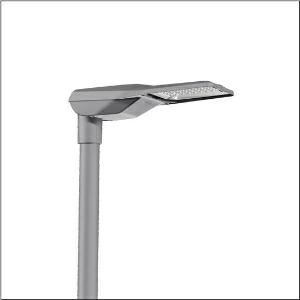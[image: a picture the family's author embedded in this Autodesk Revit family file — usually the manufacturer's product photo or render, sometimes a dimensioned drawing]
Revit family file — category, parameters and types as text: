
# Revit family: streetlight_sl_21_iq_mini___st0_8a_5xe2c31d08hb_f94e
name_source: partatom
category: Lighting Fixtures
units: mm (PartAtom-declared; Revit-internal decimal feet)

## family parameters
Cut with Voids When Loaded = No
Host = Face
Light Source = No
Part Type = Normal
Room Calculation Point = No
Round Connector Dimension = Use Diameter
Shared = No

## types (1)
- --- (1 x LED, 9450 lm, 70.9 W, 3000K)
    Apparent Load = 71 VA
    CIE Flux Codes = 38 75 97 100 100
    Color Rendering = 70
    Color Temperature = 3000K
    Default Elevation = 1800 mm
    Description = Streetlight SL 21 iQ mini, mast luminaire, primary light control with lens, of PMMA, primary optical cover: cover, of toughened safety glass, transparent, light distribution: ST0.8a, light emission: direct distribution, primary light characteristic: asymmetric, installation type: post-top, side-entry, LED, High Power LED, rated luminous flux: 9.450lm, luminous efficacy: 133lm/W, light colour: 730, colour temperature: 3000K, control: Auto-Match, Temp-Guard, Lumen-Switch, Night-Set, Smart-Wire, Light-Fading, Desk-Remote (wireless, voltage-free reading and setting of iQ features in the workshop via application-optimized NFC function/RFID function), optimised constant luminous flux control (CLO 2.0), presetting dimming linear, mains connection: 220..240V, AC, 50/60Hz, start of lifetime: 71W, end of service life: 75W, reduction: 31W, luminaire housing, of diecast aluminium, powder-coated, Siteco® metallic grey (DB 702S), corrosivity category C5 mid according to DIN EN ISO 12944, please order mast flange separately, inclination adjustable: 0°, 5°, 10°, 15°, sealing non-destructively replaceable, multi-level sealing system, length: 628mm, width: 235mm, height: 110mm, mast flange for spigot size: 42mm (side-entry): 5XC10008XM4, 60/48mm (side-entry/post-top): 5XC10108XM2, 76/60mm (side-entry/post-top): 5XC10108XM1, protection rating (complete): IP66, insulation class (complete): insulation class II (safety insulation), certification: CE, ENEC, ENEC+, VDE, impact resistance: IK09, permissible operating ambient temperature for outdoor applications: -40..+50°C, standard-compliant lighting for roads and squares, packaging unit: 1 piece

Light Distribution: ST0.8a
    Height = 110 mm
    Lamp = 1 x LED
    Lamp Light Flux = 9450 lm
    Lamp Power = 70.9 W
    Lamp count = 1
    Length = 625 mm
    Luminous efficacy = 133 lm/W
    Manufacturer = Siteco
    ModVariant = No
    Model = 5XE2C31D08HB
    Number of Poles = 1
    OnlyDefault = Yes
    Power Factor = 1
    Product Name = Streetlight SL 21 iQ mini | ST0.8a
    Product group = mast luminaire | pylon top
    ProductGroupID = 6100
    Protection Class = Protection class II
    Protection Degree = IP 66
    RLX_Detail_Level = 1
    RLX_Emergency_Light_Flux = 0 lm
    RLX_Emergency_Type = 0
    RLX_Emergency_Type_DB = No
    RlxData = <blob elided: 94365 chars, md5=e865df9f>
    Socket = socket
    Standby Power = 0 W
    System Light Flux = 9450 lm
    System Power = 71 W
    Type Comments = factory setting: luminous flux: 100 % | dim-lin: 254 | 711 mA
    Type Image = l_1003519.jpg
    URL = http://relux.com
    VarID = @adj_089773
    Voltage = 0 V
    Weight = 0.00 kg
    Width = 234 mm

## geometry (parser evidence)
native form markers: Blend x4, Sweep x11
no freeform markers — native parametric forms only
